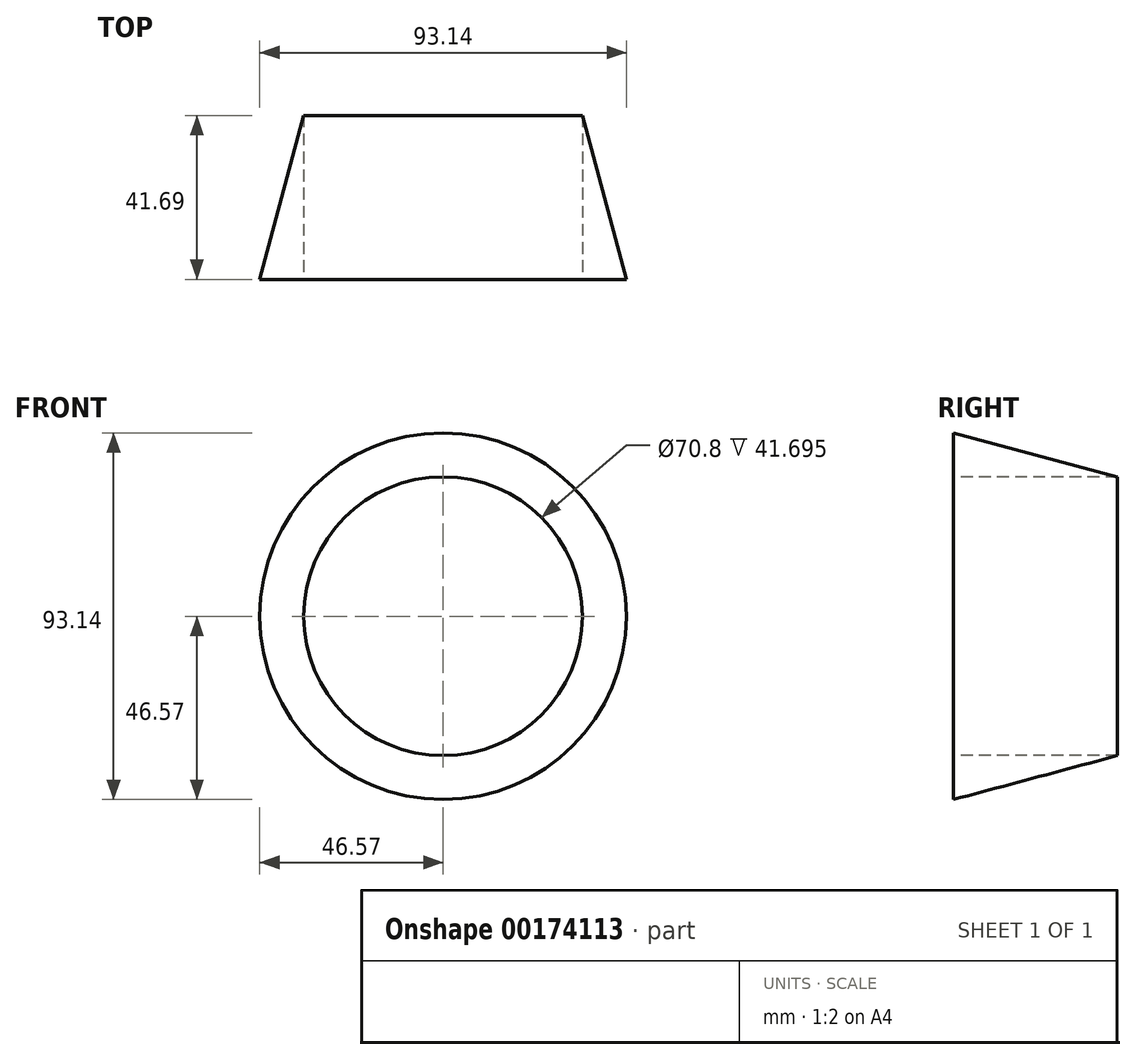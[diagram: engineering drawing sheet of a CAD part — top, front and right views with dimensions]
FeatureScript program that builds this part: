
annotation { "Feature Type Name" : "Feature", "Feature Type Description" : "" }
export const myFeature = defineFeature(function(context is Context, id is Id, definition is map)
    precondition{}
    {
        {
            var Q0;
            Q0=qCreatedBy(makeId("Front.planeOp"),FACE);
            var sketch = newSketch(context, id + "F0", { "sketchPlane" : qUnion([Q0])});
            skCircle(sketch, "E0", {"center": v(0, 0) * mm, "radius": 30.38 * mm});
            skSolve(sketch);
        }
        {
            var Q0;
            Q0 = qSketchRegion(id + "F0", true);
            extrude(context, id + "F1", {"entities" : qUnion([Q0]), "depth" : 60.45 * mm, "hasDraft" : true, "draftAngle" : 15 * degree});
        }
        {
            var Q0;
            Q0=makeQuery(id+"F1.opExtrude","CAP_FACE",FACE,{"disambiguationData":[OSD([sQuery(id+"F0.wireOp",EDGE,"E0")])],"isStart":false});
            var sketch = newSketch(context, id + "F2", { "sketchPlane" : qUnion([Q0])});
            skCircle(sketch, "E1", {"center": v(0, 0) * mm, "radius": 35.4 * mm});
            skSolve(sketch);
        }
        {
            var Q0;
            Q0=makeQuery(id+"F2.imprint","IMPRINT",FACE,{"disambiguationData":[TD([[makeQuery(id+"F2.imprint","IMPRINT",EDGE,{"derivedFrom":sQuery(id+"F2.wireOp",EDGE,"E1")}),1.0]])]});
            extrude(context, id + "F3", {"entities" : qUnion([Q0]), "operationType" : NewBodyOperationType.REMOVE, "oppositeDirection" : true, "depth" : 105.4 * mm});
        }
    });
